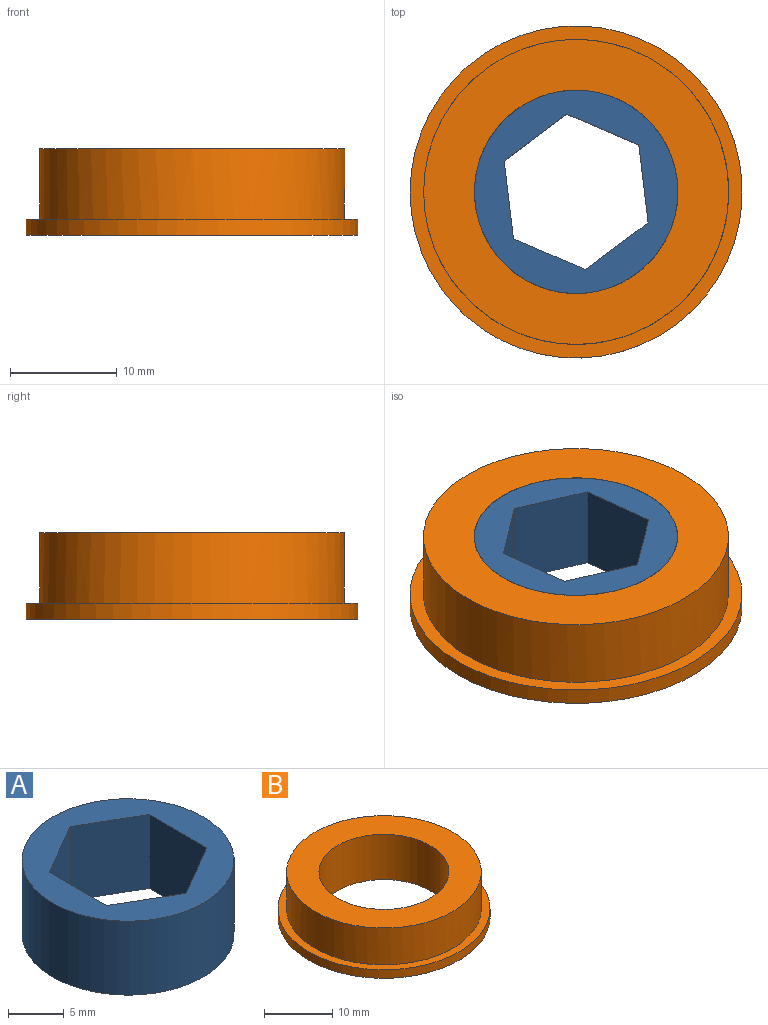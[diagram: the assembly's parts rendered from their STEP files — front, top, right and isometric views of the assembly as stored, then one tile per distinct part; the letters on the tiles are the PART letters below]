
ASSEMBLY  parts=2 mates=1
PART A: 9 faces, bbox 19.1x19.1x8.1 mm
  f0: plane 8.13x6.35mm, normal (-0.5,0.87,0), area 59.6mm2, adj f1,f5,f7,f8
  f1: plane 8.13x6.35mm, normal (0.5,0.87,0), area 59.6mm2, adj f0,f2,f7,f8
  f2: plane 8.13x7.33mm, normal (1,0,0), area 59.6mm2, adj f1,f3,f7,f8
  f3: plane 8.13x6.35mm, normal (0.5,-0.87,0), area 59.6mm2, adj f2,f4,f7,f8
  f4: plane 8.13x6.35mm, normal (-0.5,-0.87,0), area 59.6mm2, adj f3,f5,f7,f8
  f5: plane 8.13x7.33mm, normal (-1,0,0), area 59.6mm2, adj f0,f4,f7,f8
  f6: cylinder r=9.53mm len=19.05mm, axis (0,0,-1), area 486.4mm2, adj f7,f8
  f7: plane 19.05x19.05mm, normal (0,0,1), area 145.3mm2, adj f0,f1,f2,f3,f4,f5,f6
  f8: plane 19.05x19.05mm, normal (0,0,-1), area 145.3mm2, adj f0,f1,f2,f3,f4,f5,f6
PART B: 6 faces, bbox 31.1x31.1x8.1 mm
  f0: cylinder r=14.29mm len=28.58mm, axis (0,0,-1), area 592.8mm2, adj f2,f4
  f1: cylinder r=9.54mm len=19.08mm, axis (0,0,-1), area 487.1mm2, adj f2,f3
  f2: plane 28.58x28.58mm, normal (0,0,1), area 355.5mm2, adj f0,f1
  f3: plane 31.12x31.12mm, normal (0,0,-1), area 474.6mm2, adj f1,f5
  f4: plane 31.12x31.12mm, normal (0,0,1), area 119.1mm2, adj f0,f5
  f5: cylinder r=15.56mm len=31.12mm, axis (0,0,-1), area 149mm2, adj f3,f4
PLACE A rot(axis=(0,0,1),6.8deg) t=(-18.59,-6.02,3.01)mm
PLACE B t=(-18.59,-6.02,3.01)mm fixed
MATE revolute B.f1 <-> A.f6  axis (0,0,-1) through (-18.59,-6.02,11.14)mm
